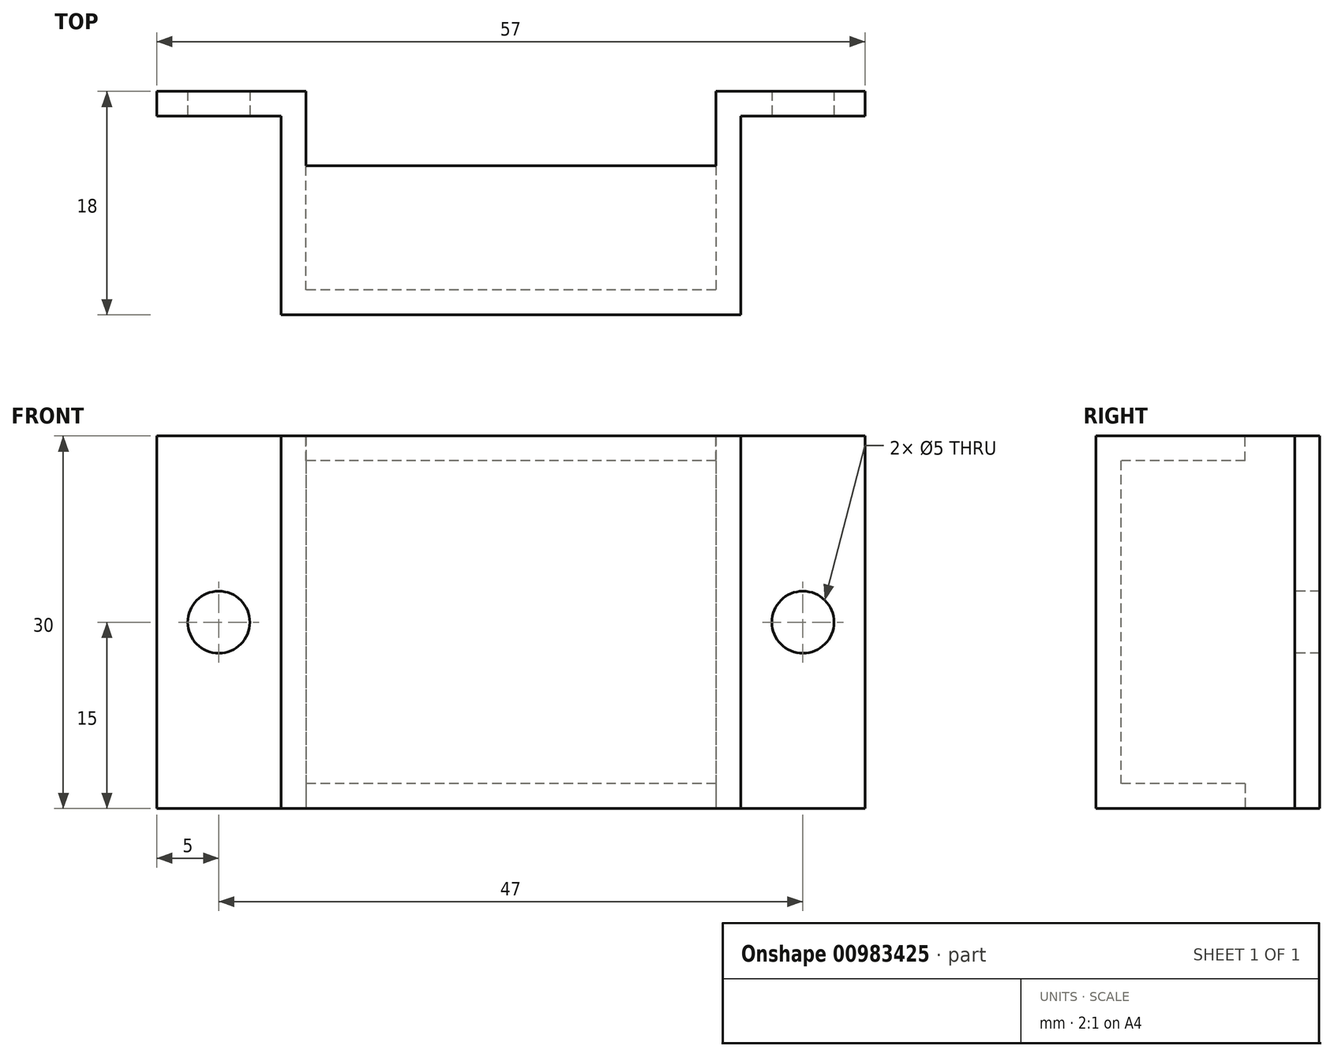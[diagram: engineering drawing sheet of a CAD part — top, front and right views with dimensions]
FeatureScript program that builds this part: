
annotation { "Feature Type Name" : "Feature", "Feature Type Description" : "" }
export const myFeature = defineFeature(function(context is Context, id is Id, definition is map)
    precondition{}
    {
        {
            var Q0;
            Q0=qCreatedBy(makeId("Top.planeOp"),FACE);
            var sketch = newSketch(context, id + "F0", { "sketchPlane" : qUnion([Q0])});
            skLineSegment(sketch, "E0", {"start": v(0, 0) * mm, "end": v(-33, 0) * mm});
            skLineSegment(sketch, "E1", {"start": v(-33, 0) * mm, "end": v(-33, 16) * mm});
            skLineSegment(sketch, "E2", {"start": v(-33, 16) * mm, "end": v(-45, 16) * mm});
            skLineSegment(sketch, "E3", {"start": v(-45, 16) * mm, "end": v(-45, 14) * mm});
            skLineSegment(sketch, "E4", {"start": v(-45, 14) * mm, "end": v(-35, 14) * mm});
            skLineSegment(sketch, "E5", {"start": v(-35, 14) * mm, "end": v(-35, -2) * mm});
            skLineSegment(sketch, "E6", {"start": v(-35, -2) * mm, "end": v(2, -2) * mm});
            skLineSegment(sketch, "E7", {"start": v(2, -2) * mm, "end": v(2, 14) * mm});
            skLineSegment(sketch, "E8", {"start": v(2, 14) * mm, "end": v(12, 14) * mm});
            skLineSegment(sketch, "E9", {"start": v(12, 14) * mm, "end": v(12, 16) * mm});
            skLineSegment(sketch, "E10", {"start": v(12, 16) * mm, "end": v(0, 16) * mm});
            skLineSegment(sketch, "E11", {"start": v(0, 16) * mm, "end": v(0, 0) * mm});
            skSolve(sketch);
        }
        {
            var Q0;
            Q0=makeQuery(id+"F0.imprint","IMPRINT",FACE,{"disambiguationData":[TD([[makeQuery(id+"F0.imprint","IMPRINT",EDGE,{"derivedFrom":sQuery(id+"F0.wireOp",EDGE,"E0")}),1.0]])]});
            extrude(context, id + "F1", {"entities" : qUnion([Q0]), "depth" : 30 * mm, "offsetDistance" : 25 * mm});
        }
        {
            var Q0;
            Q0=makeQuery(id+"F1.opExtrude","SWEPT_FACE",FACE,{"disambiguationData":[OSD([sQuery(id+"F0.wireOp",EDGE,"E4")])]});
            var sketch = newSketch(context, id + "F2", { "sketchPlane" : qUnion([Q0])});
            skPoint(sketch, "E12.oppositeSnap0", {"position": v(-40, 30) * mm});
            skLineSegment(sketch, "E12.bottom", {"start": v(-45, 30) * mm, "end": v(-40, 30) * mm, "construction": true});
            skLineSegment(sketch, "E12.top", {"start": v(-45, 15) * mm, "end": v(-40, 15) * mm, "construction": true});
            skLineSegment(sketch, "E12.left", {"start": v(-45, 30) * mm, "end": v(-45, 15) * mm, "construction": true});
            skLineSegment(sketch, "E12.right", {"start": v(-40, 30) * mm, "end": v(-40, 15) * mm, "construction": true});
            skCircle(sketch, "E13", {"center": v(-40, 15) * mm, "radius": 2.5 * mm});
            skSolve(sketch);
        }
        {
            var Q0;
            Q0 = qSketchRegion(id + "F2", true);
            extrude(context, id + "F3", {"entities" : qUnion([Q0]), "operationType" : NewBodyOperationType.REMOVE, "oppositeDirection" : true, "depth" : 25 * mm, "offsetDistance" : 25 * mm});
        }
        {
            var Q0;
            Q0=makeQuery(id+"F1.opExtrude","SWEPT_FACE",FACE,{"disambiguationData":[OSD([sQuery(id+"F0.wireOp",EDGE,"E8")])]});
            var sketch = newSketch(context, id + "F4", { "sketchPlane" : qUnion([Q0])});
            skLineSegment(sketch, "E14.bottom", {"start": v(12, 30) * mm, "end": v(7, 30) * mm, "construction": true});
            skLineSegment(sketch, "E14.top", {"start": v(12, 15) * mm, "end": v(7, 15) * mm, "construction": true});
            skLineSegment(sketch, "E14.left", {"start": v(12, 30) * mm, "end": v(12, 15) * mm, "construction": true});
            skLineSegment(sketch, "E14.right", {"start": v(7, 30) * mm, "end": v(7, 15) * mm, "construction": true});
            skCircle(sketch, "E15", {"center": v(7, 15) * mm, "radius": 2.5 * mm});
            skSolve(sketch);
        }
        {
            var Q0;
            Q0=makeQuery(id+"F4.imprint","IMPRINT",FACE,{"disambiguationData":[TD([[makeQuery(id+"F4.imprint","IMPRINT",EDGE,{"derivedFrom":sQuery(id+"F4.wireOp",EDGE,"E15")}),1.0]])]});
            extrude(context, id + "F5", {"entities" : qUnion([Q0]), "operationType" : NewBodyOperationType.REMOVE, "oppositeDirection" : true, "depth" : 25 * mm, "offsetDistance" : 25 * mm});
        }
        {
            var Q0;
            Q0=makeQuery(id+"F1.opExtrude","CAP_FACE",FACE,{"disambiguationData":[OSD([sQuery(id+"F0.wireOp",EDGE,"E0"),sQuery(id+"F0.wireOp",EDGE,"E1"),sQuery(id+"F0.wireOp",EDGE,"E2"),sQuery(id+"F0.wireOp",EDGE,"E3"),sQuery(id+"F0.wireOp",EDGE,"E4"),sQuery(id+"F0.wireOp",EDGE,"E5"),sQuery(id+"F0.wireOp",EDGE,"E6"),sQuery(id+"F0.wireOp",EDGE,"E7"),sQuery(id+"F0.wireOp",EDGE,"E8"),sQuery(id+"F0.wireOp",EDGE,"E9"),sQuery(id+"F0.wireOp",EDGE,"E10"),sQuery(id+"F0.wireOp",EDGE,"E11")])],"isStart":true});
            var sketch = newSketch(context, id + "F6", { "sketchPlane" : qUnion([Q0])});
            skLineSegment(sketch, "E16.bottom", {"start": v(-33, 0) * mm, "end": v(0, 0) * mm});
            skLineSegment(sketch, "E16.top", {"start": v(-33, -10) * mm, "end": v(0, -10) * mm});
            skLineSegment(sketch, "E16.left", {"start": v(-33, 0) * mm, "end": v(-33, -10) * mm});
            skLineSegment(sketch, "E16.right", {"start": v(0, 0) * mm, "end": v(0, -10) * mm});
            skSolve(sketch);
        }
        {
            var Q0;
            Q0=makeQuery(id+"F6.imprint","IMPRINT",FACE,{"disambiguationData":[TD([[makeQuery(id+"F6.imprint","IMPRINT",EDGE,{"derivedFrom":sQuery(id+"F6.wireOp",EDGE,"E16.bottom")}),1.0]])]});
            extrude(context, id + "F7", {"entities" : qUnion([Q0]), "operationType" : NewBodyOperationType.ADD, "oppositeDirection" : true, "depth" : 2 * mm, "offsetDistance" : 25 * mm});
        }
        {
            var Q0;
            Q0=makeQuery(id+"F1.opExtrude","CAP_FACE",FACE,{"disambiguationData":[OSD([sQuery(id+"F0.wireOp",EDGE,"E0"),sQuery(id+"F0.wireOp",EDGE,"E1"),sQuery(id+"F0.wireOp",EDGE,"E2"),sQuery(id+"F0.wireOp",EDGE,"E3"),sQuery(id+"F0.wireOp",EDGE,"E4"),sQuery(id+"F0.wireOp",EDGE,"E5"),sQuery(id+"F0.wireOp",EDGE,"E6"),sQuery(id+"F0.wireOp",EDGE,"E7"),sQuery(id+"F0.wireOp",EDGE,"E8"),sQuery(id+"F0.wireOp",EDGE,"E9"),sQuery(id+"F0.wireOp",EDGE,"E10"),sQuery(id+"F0.wireOp",EDGE,"E11")])],"isStart":false});
            var sketch = newSketch(context, id + "F8", { "sketchPlane" : qUnion([Q0])});
            skLineSegment(sketch, "E17.bottom", {"start": v(0, 0) * mm, "end": v(-33, 0) * mm});
            skLineSegment(sketch, "E17.top", {"start": v(0, 10) * mm, "end": v(-33, 10) * mm});
            skLineSegment(sketch, "E17.left", {"start": v(0, 0) * mm, "end": v(0, 10) * mm});
            skLineSegment(sketch, "E17.right", {"start": v(-33, 0) * mm, "end": v(-33, 10) * mm});
            skSolve(sketch);
        }
        {
            var Q0;
            Q0=makeQuery(id+"F8.imprint","IMPRINT",FACE,{"disambiguationData":[TD([[makeQuery(id+"F8.imprint","IMPRINT",EDGE,{"derivedFrom":sQuery(id+"F8.wireOp",EDGE,"E17.bottom")}),-1.0]])]});
            extrude(context, id + "F9", {"entities" : qUnion([Q0]), "operationType" : NewBodyOperationType.ADD, "oppositeDirection" : true, "depth" : 2 * mm, "offsetDistance" : 25 * mm});
        }
    });
